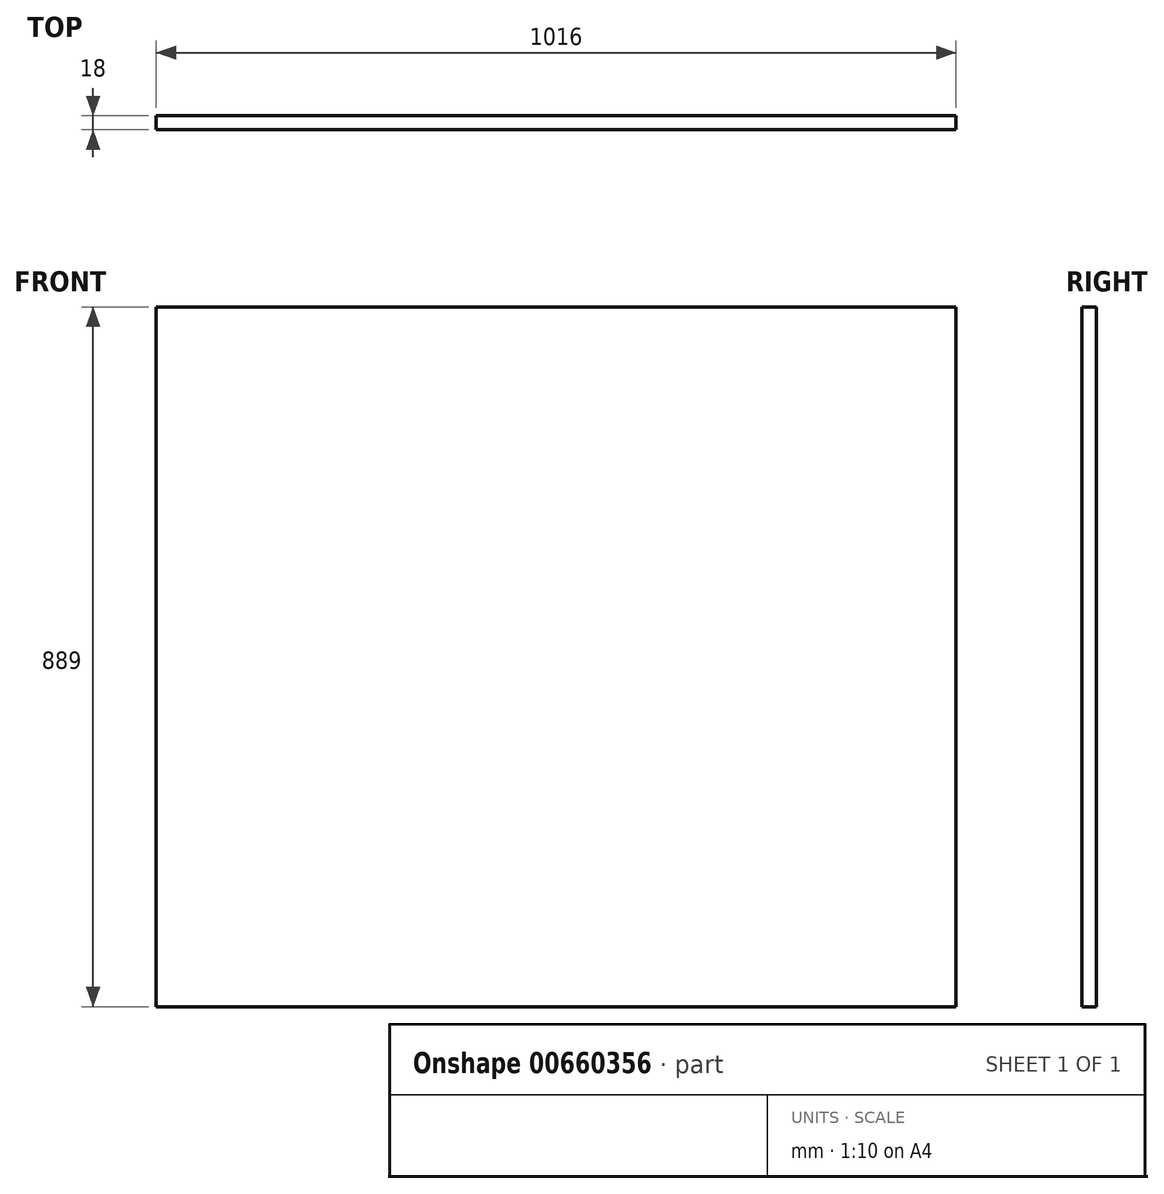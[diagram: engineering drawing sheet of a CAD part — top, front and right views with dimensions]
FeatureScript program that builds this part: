
annotation { "Feature Type Name" : "Feature", "Feature Type Description" : "" }
export const myFeature = defineFeature(function(context is Context, id is Id, definition is map)
    precondition{}
    {
        {
            var Q0;
            Q0=qCreatedBy(makeId("Front.planeOp"),FACE);
            var sketch = newSketch(context, id + "F0", { "sketchPlane" : qUnion([Q0])});
            skLineSegment(sketch, "E0.bottom", {"start": v(505.5, 443.82) * mm, "end": v(-510.5, 443.82) * mm});
            skLineSegment(sketch, "E0.top", {"start": v(505.5, -445.18) * mm, "end": v(-510.5, -445.18) * mm});
            skLineSegment(sketch, "E0.left", {"start": v(505.5, 443.82) * mm, "end": v(505.5, -445.18) * mm});
            skLineSegment(sketch, "E0.right", {"start": v(-510.5, 443.82) * mm, "end": v(-510.5, -445.18) * mm});
            skPoint(sketch, "E0.middle", {"position": v(-2.5, -0.68) * mm});
            skSolve(sketch);
        }
        {
            var Q0;
            Q0=makeQuery(id+"F0.imprint","IMPRINT",FACE,{"disambiguationData":[TD([[makeQuery(id+"F0.imprint","IMPRINT",EDGE,{"derivedFrom":sQuery(id+"F0.wireOp",EDGE,"E0.bottom")}),1.0]])]});
            extrude(context, id + "F1", {"entities" : qUnion([Q0]), "depth" : 18 * mm, "offsetDistance" : 25 * mm});
        }
    });
